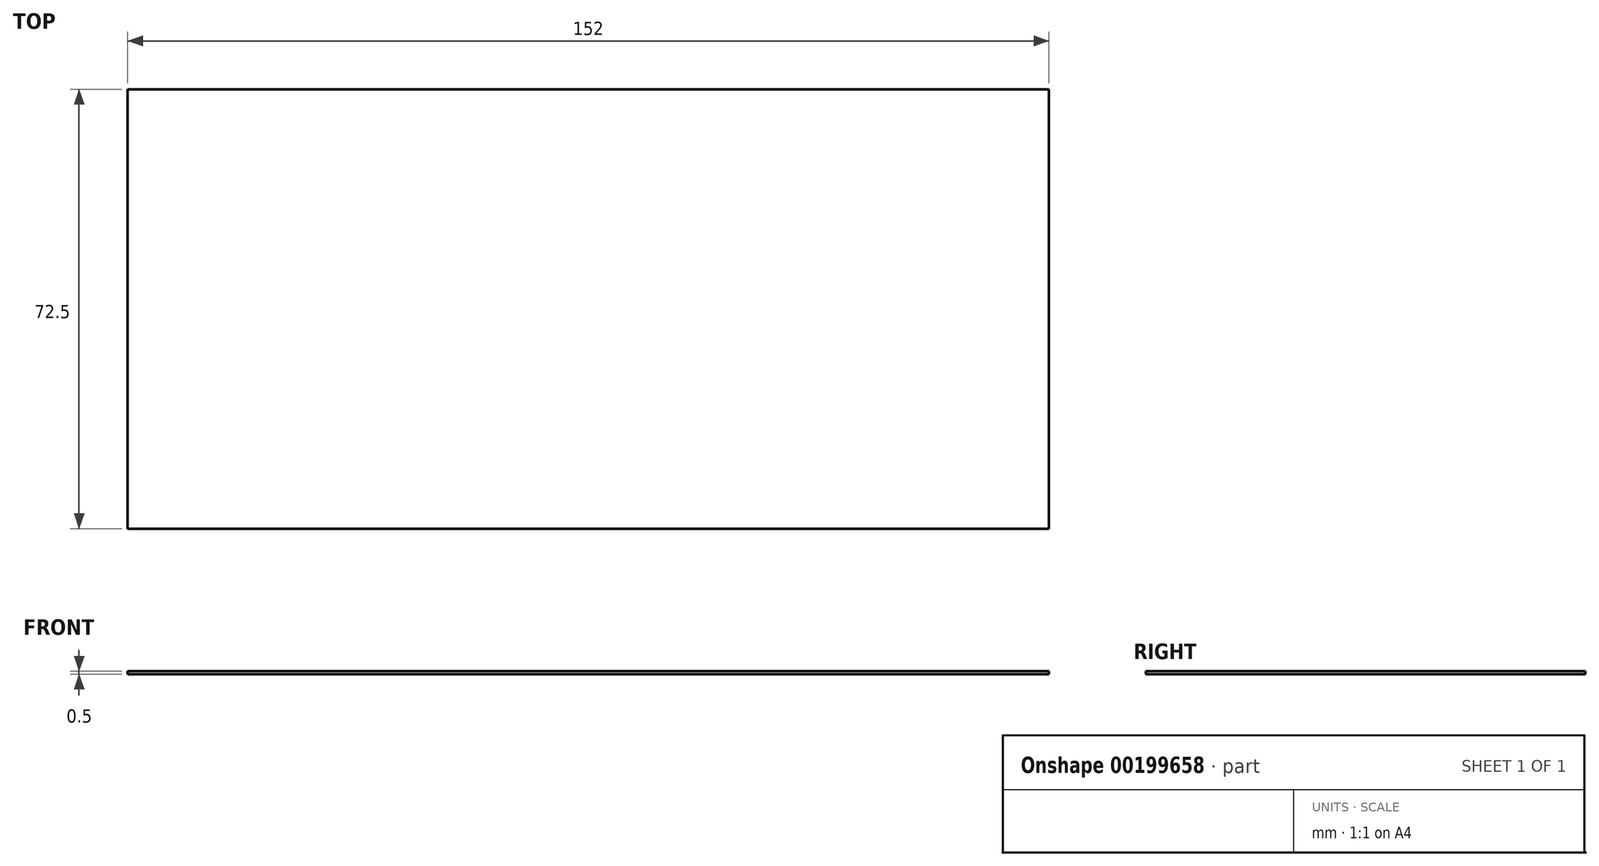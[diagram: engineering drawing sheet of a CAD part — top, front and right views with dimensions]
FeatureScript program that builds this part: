
annotation { "Feature Type Name" : "Feature", "Feature Type Description" : "" }
export const myFeature = defineFeature(function(context is Context, id is Id, definition is map)
    precondition{}
    {
        {
            var Q0;
            Q0=qCreatedBy(makeId("Top.planeOp"),FACE);
            var sketch = newSketch(context, id + "F0", { "sketchPlane" : qUnion([Q0])});
            skLineSegment(sketch, "E0.bottom", {"start": v(-76, -36.25) * mm, "end": v(76, -36.25) * mm});
            skLineSegment(sketch, "E0.top", {"start": v(-76, 36.25) * mm, "end": v(76, 36.25) * mm});
            skLineSegment(sketch, "E0.left", {"start": v(-76, -36.25) * mm, "end": v(-76, 36.25) * mm});
            skLineSegment(sketch, "E0.right", {"start": v(76, -36.25) * mm, "end": v(76, 36.25) * mm});
            skPoint(sketch, "E0.middle", {"position": v(0, 0) * mm});
            skSolve(sketch);
        }
        {
            var Q0;
            Q0=makeQuery(id+"F0.imprint","IMPRINT",FACE,{"disambiguationData":[TD([[makeQuery(id+"F0.imprint","IMPRINT",EDGE,{"derivedFrom":sQuery(id+"F0.wireOp",EDGE,"E0.bottom")}),1.0]])]});
            extrude(context, id + "F1", {"entities" : qUnion([Q0]), "depth" : 0.5 * mm});
        }
    });
